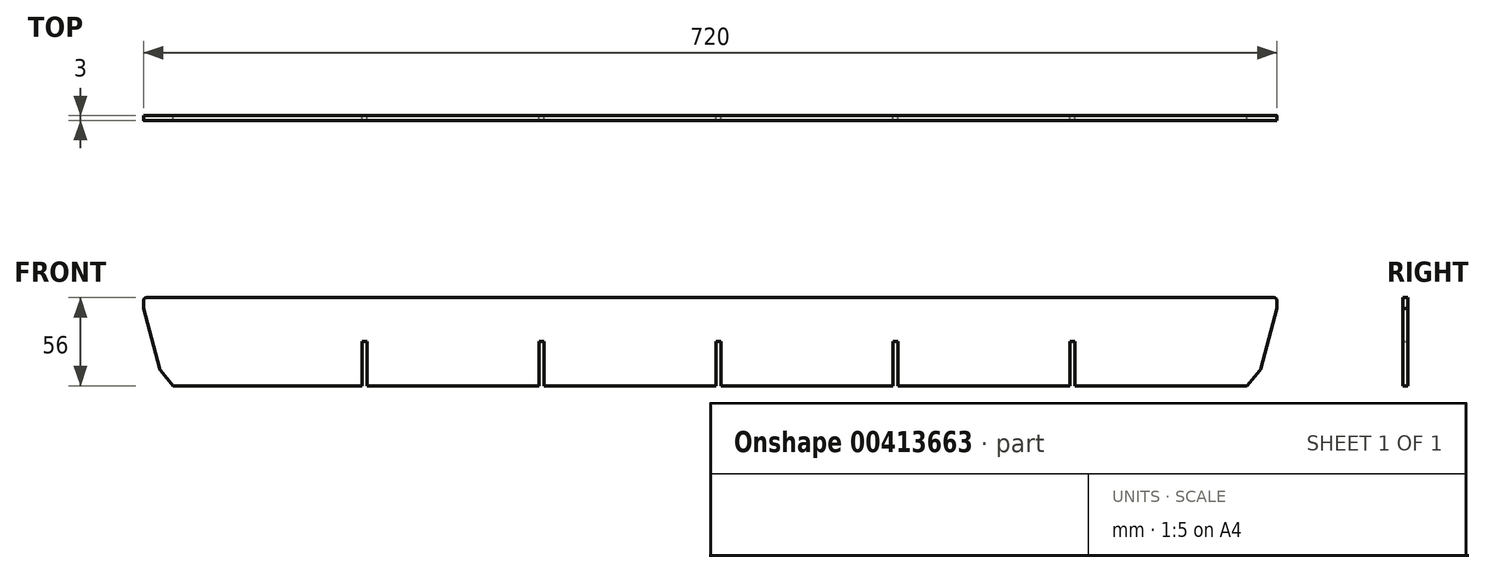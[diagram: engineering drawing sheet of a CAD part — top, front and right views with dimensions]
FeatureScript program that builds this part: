
annotation { "Feature Type Name" : "Feature", "Feature Type Description" : "" }
export const myFeature = defineFeature(function(context is Context, id is Id, definition is map)
    precondition{}
    {
        {
            var Q0;
            Q0=qCreatedBy(makeId("Front.planeOp"),FACE);
            var sketch = newSketch(context, id + "F0", { "sketchPlane" : qUnion([Q0])});
            skLineSegment(sketch, "E0.bottom", {"start": v(0, 0) * mm, "end": v(3.8, 0) * mm});
            skLineSegment(sketch, "E0.top", {"start": v(0, 56) * mm, "end": v(358, 56) * mm});
            skLineSegment(sketch, "E0.right", {"start": v(360, 49) * mm, "end": v(360, 54) * mm});
            skArc(sketch, "E1", {"start": v(360, 54) * mm, "mid": v(359.41, 55.41) * mm, "end": v(358, 56) * mm});
            skLineSegment(sketch, "E2", {"start": v(341, 0) * mm, "end": v(349.2, 9.77) * mm});
            skPoint(sketch, "E3", {"position": v(360, 49) * mm});
            skLineSegment(sketch, "E4", {"start": v(360, 49) * mm, "end": v(349.8, 10.92) * mm});
            skArc(sketch, "E5", {"start": v(349.2, 9.77) * mm, "mid": v(349.56, 10.31) * mm, "end": v(349.8, 10.92) * mm});
            skLineSegment(sketch, "E6.MirrorCS", {"start": v(0, 56) * mm, "end": v(-358, 56) * mm});
            skLineSegment(sketch, "E7.MirrorCS", {"start": v(0, 0) * mm, "end": v(-105.6, 0) * mm});
            skLineSegment(sketch, "E8.MirrorCS", {"start": v(-341, 0) * mm, "end": v(-349.2, 9.77) * mm});
            skArc(sketch, "E9.MirrorCS", {"start": v(-349.2, 9.77) * mm, "mid": v(-349.56, 10.31) * mm, "end": v(-349.8, 10.92) * mm});
            skLineSegment(sketch, "E10.MirrorCS", {"start": v(-360, 49) * mm, "end": v(-349.8, 10.92) * mm});
            skLineSegment(sketch, "E11.MirrorCS", {"start": v(-360, 49) * mm, "end": v(-360, 54) * mm});
            skArc(sketch, "E12.MirrorCS", {"start": v(-360, 54) * mm, "mid": v(-359.41, 55.41) * mm, "end": v(-358, 56) * mm});
            skPoint(sketch, "E13.orphan", {"position": v(-360, 0) * mm});
            skPoint(sketch, "E14.orphan", {"position": v(360, 0) * mm});
            skLineSegment(sketch, "E15.top", {"start": v(228.6, 28) * mm, "end": v(231.6, 28) * mm});
            skLineSegment(sketch, "E15.left", {"start": v(228.6, 0) * mm, "end": v(228.6, 28) * mm});
            skLineSegment(sketch, "E15.right", {"start": v(231.6, 0) * mm, "end": v(231.6, 28) * mm});
            skLineSegment(sketch, "E16.bottom", {"start": v(-221, 28) * mm, "end": v(-218, 28) * mm});
            skLineSegment(sketch, "E16.left", {"start": v(-221, 28) * mm, "end": v(-221, 0) * mm});
            skLineSegment(sketch, "E16.right", {"start": v(-218, 28) * mm, "end": v(-218, 0) * mm});
            skLineSegment(sketch, "E17.bottom", {"start": v(116.2, 28) * mm, "end": v(119.2, 28) * mm});
            skLineSegment(sketch, "E17.left", {"start": v(116.2, 28) * mm, "end": v(116.2, 0) * mm});
            skLineSegment(sketch, "E17.right", {"start": v(119.2, 28) * mm, "end": v(119.2, 0) * mm});
            skLineSegment(sketch, "E18.bottom", {"start": v(3.8, 28) * mm, "end": v(6.8, 28) * mm});
            skLineSegment(sketch, "E18.left", {"start": v(3.8, 28) * mm, "end": v(3.8, 0) * mm});
            skLineSegment(sketch, "E18.right", {"start": v(6.8, 28) * mm, "end": v(6.8, 0) * mm});
            skLineSegment(sketch, "E19.bottom", {"start": v(-108.6, 28) * mm, "end": v(-105.6, 28) * mm});
            skLineSegment(sketch, "E19.left", {"start": v(-108.6, 28) * mm, "end": v(-108.6, 0) * mm});
            skLineSegment(sketch, "E19.right", {"start": v(-105.6, 28) * mm, "end": v(-105.6, 0) * mm});
            skLineSegment(sketch, "E20.trimOffspring", {"start": v(-221, 0) * mm, "end": v(-341, 0) * mm});
            skLineSegment(sketch, "E21.trimOffspring", {"start": v(-108.6, 0) * mm, "end": v(-218, 0) * mm});
            skLineSegment(sketch, "E22.trimOffspring", {"start": v(6.8, 0) * mm, "end": v(116.2, 0) * mm});
            skLineSegment(sketch, "E23.trimOffspring", {"start": v(119.2, 0) * mm, "end": v(228.6, 0) * mm});
            skLineSegment(sketch, "E24.trimOffspring", {"start": v(231.6, 0) * mm, "end": v(341, 0) * mm});
            skSolve(sketch);
        }
        {
            var Q0;
            Q0=makeQuery(id+"F0.imprint","IMPRINT",FACE,{"disambiguationData":[TD([[makeQuery(id+"F0.imprint","IMPRINT",EDGE,{"derivedFrom":sQuery(id+"F0.wireOp",EDGE,"E0.bottom")}),1.0]])]});
            extrude(context, id + "F1", {"entities" : qUnion([Q0]), "endBound" : BoundingType.SYMMETRIC, "depth" : 3 * mm});
        }
    });
